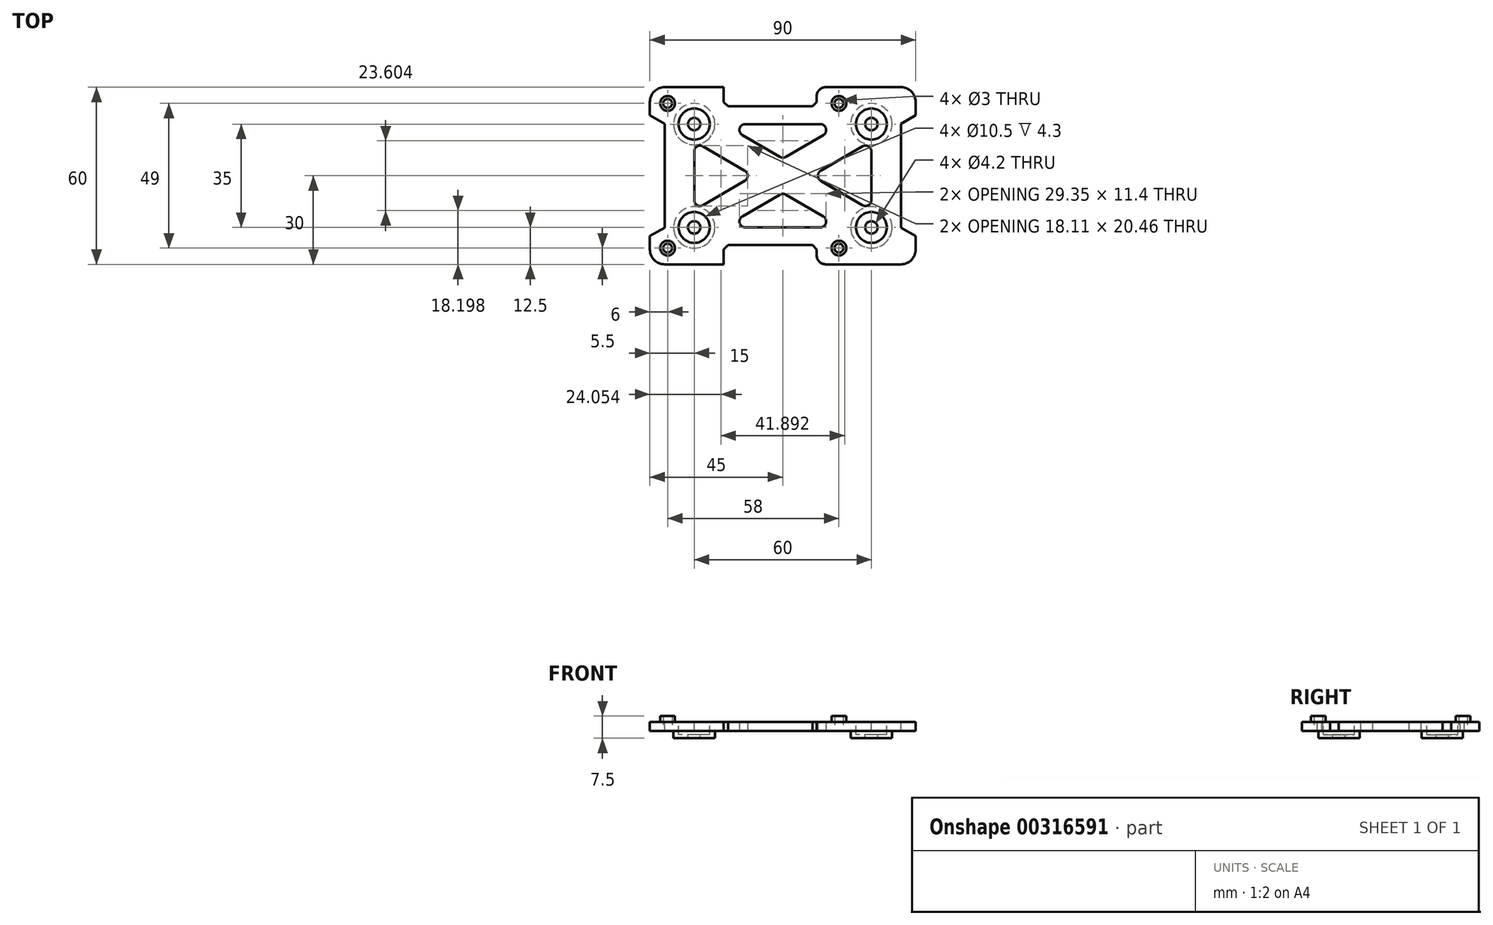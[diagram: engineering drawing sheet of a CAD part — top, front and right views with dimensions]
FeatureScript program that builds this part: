
annotation { "Feature Type Name" : "Feature", "Feature Type Description" : "" }
export const myFeature = defineFeature(function(context is Context, id is Id, definition is map)
    precondition{}
    {
        {
            var Q0;
            Q0=qCreatedBy(makeId("Top.planeOp"),FACE);
            var sketch = newSketch(context, id + "F0", { "sketchPlane" : qUnion([Q0])});
            skLineSegment(sketch, "E0.bottom", {"start": v(-45, 30) * mm, "end": v(45, 30) * mm});
            skLineSegment(sketch, "E0.top", {"start": v(-45, -30) * mm, "end": v(45, -30) * mm});
            skLineSegment(sketch, "E0.left", {"start": v(-45, 30) * mm, "end": v(-45, -30) * mm});
            skLineSegment(sketch, "E0.right", {"start": v(45, 30) * mm, "end": v(45, -30) * mm});
            skPoint(sketch, "E1", {"position": v(-45, 0) * mm});
            skPoint(sketch, "E2", {"position": v(0, 30) * mm});
            skSolve(sketch);
        }
        {
            var Q0;
            Q0=makeQuery(id+"F0.imprint","IMPRINT",FACE,{"disambiguationData":[TD([[makeQuery(id+"F0.imprint","IMPRINT",EDGE,{"derivedFrom":sQuery(id+"F0.wireOp",EDGE,"E0.bottom")}),-1.0]])]});
            extrude(context, id + "F1", {"entities" : qUnion([Q0]), "depth" : 3 * mm});
        }
        {
            var Q0;
            Q0=makeQuery(id+"F1.opExtrude","CAP_FACE",FACE,{"disambiguationData":[OSD([sQuery(id+"F0.wireOp",EDGE,"E0.bottom"),sQuery(id+"F0.wireOp",EDGE,"E0.top"),sQuery(id+"F0.wireOp",EDGE,"E0.left"),sQuery(id+"F0.wireOp",EDGE,"E0.right")])],"isStart":false});
            var sketch = newSketch(context, id + "F2", { "sketchPlane" : qUnion([Q0])});
            skLineSegment(sketch, "E3.bottom", {"start": v(-39, 24.5) * mm, "end": v(19, 24.5) * mm, "construction": true});
            skLineSegment(sketch, "E3.top", {"start": v(-39, -24.5) * mm, "end": v(19, -24.5) * mm, "construction": true});
            skLineSegment(sketch, "E3.left", {"start": v(-39, 24.5) * mm, "end": v(-39, -24.5) * mm, "construction": true});
            skLineSegment(sketch, "E3.right", {"start": v(19, 24.5) * mm, "end": v(19, -24.5) * mm, "construction": true});
            skLineSegment(sketch, "E4.bottom", {"start": v(-42.5, 28) * mm, "end": v(42.5, 28) * mm, "construction": true});
            skLineSegment(sketch, "E4.top", {"start": v(-42.5, -28) * mm, "end": v(42.5, -28) * mm, "construction": true});
            skLineSegment(sketch, "E4.left", {"start": v(-42.5, 28) * mm, "end": v(-42.5, -28) * mm, "construction": true});
            skLineSegment(sketch, "E4.right", {"start": v(42.5, 28) * mm, "end": v(42.5, -28) * mm, "construction": true});
            skPoint(sketch, "E5", {"position": v(-42.5, 0) * mm});
            skPoint(sketch, "E6", {"position": v(-39, 0) * mm});
            skPoint(sketch, "E7", {"position": v(0, 28) * mm});
            skCircle(sketch, "E8", {"center": v(-39, 24.5) * mm, "radius": 2.5 * mm});
            skCircle(sketch, "E9", {"center": v(19, 24.5) * mm, "radius": 2.5 * mm});
            skCircle(sketch, "E10", {"center": v(19, -24.5) * mm, "radius": 2.5 * mm});
            skCircle(sketch, "E11", {"center": v(-39, -24.5) * mm, "radius": 2.5 * mm});
            skSolve(sketch);
        }
        {
            var Q0;
            Q0=makeQuery(id+"F2.imprint","IMPRINT",FACE,{"disambiguationData":[TD([[makeQuery(id+"F2.imprint","IMPRINT",EDGE,{"derivedFrom":sQuery(id+"F2.wireOp",EDGE,"E8")}),1.0]])]});
            var Q1;
            Q1=makeQuery(id+"F2.imprint","IMPRINT",FACE,{"disambiguationData":[TD([[makeQuery(id+"F2.imprint","IMPRINT",EDGE,{"derivedFrom":sQuery(id+"F2.wireOp",EDGE,"E9")}),1.0]])]});
            var Q2;
            Q2=makeQuery(id+"F2.imprint","IMPRINT",FACE,{"disambiguationData":[TD([[makeQuery(id+"F2.imprint","IMPRINT",EDGE,{"derivedFrom":sQuery(id+"F2.wireOp",EDGE,"E10")}),1.0]])]});
            var Q3;
            Q3=makeQuery(id+"F2.imprint","IMPRINT",FACE,{"disambiguationData":[TD([[makeQuery(id+"F2.imprint","IMPRINT",EDGE,{"derivedFrom":sQuery(id+"F2.wireOp",EDGE,"E11")}),1.0]])]});
            extrude(context, id + "F3", {"entities" : qUnion([Q0, Q1, Q2, Q3]), "operationType" : NewBodyOperationType.ADD, "depth" : 2 * mm, "offsetDistance" : 25 * mm});
        }
        {
            var Q0;
            Q0=makeQuery(id+"F1.opExtrude","CAP_FACE",FACE,{"disambiguationData":[OSD([sQuery(id+"F0.wireOp",EDGE,"E0.bottom"),sQuery(id+"F0.wireOp",EDGE,"E0.top"),sQuery(id+"F0.wireOp",EDGE,"E0.left"),sQuery(id+"F0.wireOp",EDGE,"E0.right")])],"isStart":true});
            var sketch = newSketch(context, id + "F4", { "sketchPlane" : qUnion([Q0])});
            skCircle(sketch, "E12.0.0", {"center": v(-39, -24.5) * mm, "radius": 2.5 * mm, "construction": true});
            skCircle(sketch, "E13.0.0", {"center": v(-39, 24.5) * mm, "radius": 2.5 * mm, "construction": true});
            skCircle(sketch, "E14.0.0", {"center": v(19, 24.5) * mm, "radius": 2.5 * mm, "construction": true});
            skCircle(sketch, "E15.0", {"center": v(19, -24.5) * mm, "radius": 2.5 * mm, "construction": true});
            skCircle(sketch, "E16", {"center": v(-39, 24.5) * mm, "radius": 1.5 * mm});
            skCircle(sketch, "E17", {"center": v(19, 24.5) * mm, "radius": 1.5 * mm});
            skCircle(sketch, "E18", {"center": v(19, -24.5) * mm, "radius": 1.5 * mm});
            skCircle(sketch, "E19", {"center": v(-39, -24.5) * mm, "radius": 1.5 * mm});
            skSolve(sketch);
        }
        {
            var Q0;
            Q0=makeQuery(id+"F4.imprint","IMPRINT",FACE,{"disambiguationData":[TD([[makeQuery(id+"F4.imprint","IMPRINT",EDGE,{"derivedFrom":sQuery(id+"F4.wireOp",EDGE,"E16")}),1.0]])]});
            var Q1;
            Q1=makeQuery(id+"F4.imprint","IMPRINT",FACE,{"disambiguationData":[TD([[makeQuery(id+"F4.imprint","IMPRINT",EDGE,{"derivedFrom":sQuery(id+"F4.wireOp",EDGE,"E17")}),1.0]])]});
            var Q2;
            Q2=makeQuery(id+"F4.imprint","IMPRINT",FACE,{"disambiguationData":[TD([[makeQuery(id+"F4.imprint","IMPRINT",EDGE,{"derivedFrom":sQuery(id+"F4.wireOp",EDGE,"E18")}),1.0]])]});
            var Q3;
            Q3=makeQuery(id+"F4.imprint","IMPRINT",FACE,{"disambiguationData":[TD([[makeQuery(id+"F4.imprint","IMPRINT",EDGE,{"derivedFrom":sQuery(id+"F4.wireOp",EDGE,"E19")}),1.0]])]});
            var Q4;
            Q4=makeQuery(id+"F3.opExtrude","CAP_FACE",FACE,{"disambiguationData":[OSD([sQuery(id+"F2.wireOp",EDGE,"E11")])],"isStart":false});
            extrude(context, id + "F5", {"entities" : qUnion([Q0, Q1, Q2, Q3]), "operationType" : NewBodyOperationType.REMOVE, "endBound" : BoundingType.UP_TO_SURFACE, "oppositeDirection" : true, "endBoundEntityFace" : qUnion([Q4]), "depth" : 25 * mm});
        }
        {
            var Q0;
            Q0=makeQuery(id+"F1.opExtrude","CAP_FACE",FACE,{"disambiguationData":[OSD([sQuery(id+"F0.wireOp",EDGE,"E0.bottom"),sQuery(id+"F0.wireOp",EDGE,"E0.top"),sQuery(id+"F0.wireOp",EDGE,"E0.left"),sQuery(id+"F0.wireOp",EDGE,"E0.right")])],"isStart":true});
            var sketch = newSketch(context, id + "F6", { "sketchPlane" : qUnion([Q0])});
            skLineSegment(sketch, "E20.bottom", {"start": v(30, -17.5) * mm, "end": v(-30, -17.5) * mm, "construction": true});
            skLineSegment(sketch, "E20.top", {"start": v(30, 17.5) * mm, "end": v(-30, 17.5) * mm, "construction": true});
            skLineSegment(sketch, "E20.left", {"start": v(30, -17.5) * mm, "end": v(30, 17.5) * mm, "construction": true});
            skLineSegment(sketch, "E20.right", {"start": v(-30, -17.5) * mm, "end": v(-30, 17.5) * mm, "construction": true});
            skCircle(sketch, "E21", {"center": v(30, -17.5) * mm, "radius": 7 * mm});
            skCircle(sketch, "E22", {"center": v(-30, -17.5) * mm, "radius": 7 * mm});
            skCircle(sketch, "E23", {"center": v(-30, 17.5) * mm, "radius": 7 * mm});
            skCircle(sketch, "E24", {"center": v(30, 17.5) * mm, "radius": 7 * mm});
            skPoint(sketch, "E25", {"position": v(0, -17.5) * mm});
            skPoint(sketch, "E26", {"position": v(30, 0) * mm});
            skSolve(sketch);
        }
        {
            var Q0;
            Q0=makeQuery(id+"F6.imprint","IMPRINT",FACE,{"disambiguationData":[TD([[makeQuery(id+"F6.imprint","IMPRINT",EDGE,{"derivedFrom":sQuery(id+"F6.wireOp",EDGE,"E21")}),1.0]])]});
            var Q1;
            Q1=makeQuery(id+"F6.imprint","IMPRINT",FACE,{"disambiguationData":[TD([[makeQuery(id+"F6.imprint","IMPRINT",EDGE,{"derivedFrom":sQuery(id+"F6.wireOp",EDGE,"E24")}),1.0]])]});
            var Q2;
            Q2=makeQuery(id+"F6.imprint","IMPRINT",FACE,{"disambiguationData":[TD([[makeQuery(id+"F6.imprint","IMPRINT",EDGE,{"derivedFrom":sQuery(id+"F6.wireOp",EDGE,"E22")}),1.0]])]});
            var Q3;
            Q3=makeQuery(id+"F6.imprint","IMPRINT",FACE,{"disambiguationData":[TD([[makeQuery(id+"F6.imprint","IMPRINT",EDGE,{"derivedFrom":sQuery(id+"F6.wireOp",EDGE,"E23")}),1.0]])]});
            extrude(context, id + "F7", {"entities" : qUnion([Q0, Q1, Q2, Q3]), "operationType" : NewBodyOperationType.ADD, "depth" : 2.5 * mm});
        }
        {
            var Q0;
            Q0=makeQuery(id+"F1.opExtrude","CAP_FACE",FACE,{"disambiguationData":[OSD([sQuery(id+"F0.wireOp",EDGE,"E0.bottom"),sQuery(id+"F0.wireOp",EDGE,"E0.top"),sQuery(id+"F0.wireOp",EDGE,"E0.left"),sQuery(id+"F0.wireOp",EDGE,"E0.right")])],"isStart":false});
            var sketch = newSketch(context, id + "F8", { "sketchPlane" : qUnion([Q0])});
            skCircle(sketch, "E27.0.0", {"center": v(30, 17.5) * mm, "radius": 7 * mm, "construction": true});
            skCircle(sketch, "E28.0.0", {"center": v(30, -17.5) * mm, "radius": 7 * mm, "construction": true});
            skCircle(sketch, "E29.0.0", {"center": v(-30, -17.5) * mm, "radius": 7 * mm, "construction": true});
            skCircle(sketch, "E30.0.0", {"center": v(-30, 17.5) * mm, "radius": 7 * mm, "construction": true});
            skCircle(sketch, "E31", {"center": v(30, -17.5) * mm, "radius": 5.25 * mm});
            skCircle(sketch, "E32", {"center": v(-30, -17.5) * mm, "radius": 5.25 * mm});
            skCircle(sketch, "E33", {"center": v(-30, 17.5) * mm, "radius": 5.25 * mm});
            skCircle(sketch, "E34", {"center": v(30, 17.5) * mm, "radius": 5.25 * mm});
            skCircle(sketch, "E35", {"center": v(-30, -17.5) * mm, "radius": 2.1 * mm});
            skCircle(sketch, "E36", {"center": v(30, -17.5) * mm, "radius": 2.1 * mm});
            skCircle(sketch, "E37", {"center": v(30, 17.5) * mm, "radius": 2.1 * mm});
            skCircle(sketch, "E38", {"center": v(-30, 17.5) * mm, "radius": 2.1 * mm});
            skSolve(sketch);
        }
        {
            var Q0;
            Q0=makeQuery(id+"F8.imprint","IMPRINT",FACE,{"disambiguationData":[TD([[makeQuery(id+"F8.imprint","IMPRINT",EDGE,{"derivedFrom":sQuery(id+"F8.wireOp",EDGE,"E31")}),1.0]])]});
            var Q1;
            Q1=makeQuery(id+"F8.imprint","IMPRINT",FACE,{"disambiguationData":[TD([[makeQuery(id+"F8.imprint","IMPRINT",EDGE,{"derivedFrom":sQuery(id+"F8.wireOp",EDGE,"E32")}),1.0]])]});
            var Q2;
            Q2=makeQuery(id+"F8.imprint","IMPRINT",FACE,{"disambiguationData":[TD([[makeQuery(id+"F8.imprint","IMPRINT",EDGE,{"derivedFrom":sQuery(id+"F8.wireOp",EDGE,"E33")}),1.0]])]});
            var Q3;
            Q3=makeQuery(id+"F8.imprint","IMPRINT",FACE,{"disambiguationData":[TD([[makeQuery(id+"F8.imprint","IMPRINT",EDGE,{"derivedFrom":sQuery(id+"F8.wireOp",EDGE,"E34")}),1.0]])]});
            extrude(context, id + "F9", {"entities" : qUnion([Q0, Q1, Q2, Q3]), "operationType" : NewBodyOperationType.REMOVE, "oppositeDirection" : true, "depth" : 4.3 * mm});
        }
        {
            var Q0;
            Q0=makeQuery(id+"F8.imprint","IMPRINT",FACE,{"disambiguationData":[TD([[makeQuery(id+"F8.imprint","IMPRINT",EDGE,{"derivedFrom":sQuery(id+"F8.wireOp",EDGE,"E35")}),1.0]])]});
            var Q1;
            Q1=makeQuery(id+"F8.imprint","IMPRINT",FACE,{"disambiguationData":[TD([[makeQuery(id+"F8.imprint","IMPRINT",EDGE,{"derivedFrom":sQuery(id+"F8.wireOp",EDGE,"E38")}),1.0]])]});
            var Q2;
            Q2=makeQuery(id+"F8.imprint","IMPRINT",FACE,{"disambiguationData":[TD([[makeQuery(id+"F8.imprint","IMPRINT",EDGE,{"derivedFrom":sQuery(id+"F8.wireOp",EDGE,"E37")}),1.0]])]});
            var Q3;
            Q3=makeQuery(id+"F8.imprint","IMPRINT",FACE,{"disambiguationData":[TD([[makeQuery(id+"F8.imprint","IMPRINT",EDGE,{"derivedFrom":sQuery(id+"F8.wireOp",EDGE,"E36")}),1.0]])]});
            var Q4;
            Q4=makeQuery(id+"F7.opExtrude","CAP_FACE",FACE,{"disambiguationData":[OSD([sQuery(id+"F6.wireOp",EDGE,"E23")])],"isStart":false});
            extrude(context, id + "F10", {"entities" : qUnion([Q0, Q1, Q2, Q3]), "operationType" : NewBodyOperationType.REMOVE, "endBound" : BoundingType.UP_TO_SURFACE, "oppositeDirection" : true, "endBoundEntityFace" : qUnion([Q4]), "depth" : 25 * mm});
        }
        {
            var Q0;
            Q0=makeQuery(id+"F8.imprint","IMPRINT",FACE,{"disambiguationData":[TD([[makeQuery(id+"F8.imprint","IMPRINT",EDGE,{"derivedFrom":sQuery(id+"F8.wireOp",EDGE,"E31")}),-1.0]])]});
            var sketch = newSketch(context, id + "F11", { "sketchPlane" : qUnion([Q0])});
            skCircle(sketch, "E39.0.0", {"center": v(-30, 17.5) * mm, "radius": 5.25 * mm, "construction": true});
            skCircle(sketch, "E40.0.0", {"center": v(30, 17.5) * mm, "radius": 5.25 * mm, "construction": true});
            skCircle(sketch, "E41.0.0", {"center": v(30, -17.5) * mm, "radius": 5.25 * mm, "construction": true});
            skCircle(sketch, "E42.0", {"center": v(-30, -17.5) * mm, "radius": 5.25 * mm, "construction": true});
            skLineSegment(sketch, "E43.0.0", {"start": v(45, 30) * mm, "end": v(-45, 30) * mm, "construction": true});
            skLineSegment(sketch, "E43.0.1", {"start": v(-45, 30) * mm, "end": v(-45, -30) * mm, "construction": true});
            skLineSegment(sketch, "E43.0.2", {"start": v(-45, -30) * mm, "end": v(45, -30) * mm, "construction": true});
            skLineSegment(sketch, "E43.0.3", {"start": v(45, -30) * mm, "end": v(45, 30) * mm, "construction": true});
            skLineSegment(sketch, "E44", {"start": v(-30, 17.5) * mm, "end": v(30, -17.5) * mm, "construction": true});
            skLineSegment(sketch, "E45", {"start": v(30, 17.5) * mm, "end": v(-30, -17.5) * mm, "construction": true});
            skLineSegment(sketch, "E46", {"start": v(-30, 17.5) * mm, "end": v(-30, -17.5) * mm, "construction": true});
            skLineSegment(sketch, "E47", {"start": v(30, -17.5) * mm, "end": v(-30, -17.5) * mm, "construction": true});
            skLineSegment(sketch, "E48", {"start": v(30, -17.5) * mm, "end": v(30, 17.5) * mm, "construction": true});
            skLineSegment(sketch, "E49", {"start": v(30, 17.5) * mm, "end": v(-30, 17.5) * mm, "construction": true});
            skLineSegment(sketch, "E50", {"start": v(-30, 11.71) * mm, "end": v(-30, -11.71) * mm});
            skLineSegment(sketch, "E51", {"start": v(-30, -11.71) * mm, "end": v(-9.92, 0) * mm});
            skLineSegment(sketch, "E52", {"start": v(-9.92, 0) * mm, "end": v(-30, 11.71) * mm});
            skLineSegment(sketch, "E53", {"start": v(9.92, 0) * mm, "end": v(30, 11.71) * mm});
            skLineSegment(sketch, "E54", {"start": v(30, 11.71) * mm, "end": v(30, -11.71) * mm});
            skLineSegment(sketch, "E55", {"start": v(30, -11.71) * mm, "end": v(9.92, 0) * mm});
            skLineSegment(sketch, "E56", {"start": v(-20.08, 17.5) * mm, "end": v(0, 5.79) * mm});
            skLineSegment(sketch, "E57", {"start": v(0, 5.79) * mm, "end": v(20.08, 17.5) * mm});
            skLineSegment(sketch, "E58", {"start": v(20.08, 17.5) * mm, "end": v(-20.08, 17.5) * mm});
            skLineSegment(sketch, "E59", {"start": v(-20.08, -17.5) * mm, "end": v(0, -5.79) * mm});
            skLineSegment(sketch, "E60", {"start": v(0, -5.79) * mm, "end": v(20.08, -17.5) * mm});
            skLineSegment(sketch, "E61", {"start": v(20.08, -17.5) * mm, "end": v(-20.08, -17.5) * mm});
            skLineSegment(sketch, "E62", {"start": v(-45, 20.46) * mm, "end": v(-40, 17.54) * mm});
            skLineSegment(sketch, "E63", {"start": v(-40, 17.54) * mm, "end": v(-40, -17.54) * mm});
            skLineSegment(sketch, "E64", {"start": v(-40, -17.54) * mm, "end": v(-45, -20.46) * mm});
            skLineSegment(sketch, "E65", {"start": v(-45, -20.46) * mm, "end": v(-45, 20.46) * mm});
            skLineSegment(sketch, "E66", {"start": v(45, 20.46) * mm, "end": v(40, 17.54) * mm});
            skLineSegment(sketch, "E67", {"start": v(40, 17.54) * mm, "end": v(40, -17.54) * mm});
            skLineSegment(sketch, "E68", {"start": v(40, -17.54) * mm, "end": v(45, -20.46) * mm});
            skLineSegment(sketch, "E69", {"start": v(45, -20.46) * mm, "end": v(45, 20.46) * mm});
            skPoint(sketch, "E70", {"position": v(-45, 0) * mm});
            skPoint(sketch, "E71", {"position": v(45, 0) * mm});
            skLineSegment(sketch, "E72", {"start": v(-40, 17.54) * mm, "end": v(-30, 11.71) * mm, "construction": true});
            skLineSegment(sketch, "E73", {"start": v(30, 11.71) * mm, "end": v(40, 17.54) * mm, "construction": true});
            skLineSegment(sketch, "E74.bottom", {"start": v(-20.08, 30) * mm, "end": v(11.5, 30) * mm});
            skLineSegment(sketch, "E74.top", {"start": v(-20.08, 23.5) * mm, "end": v(11.5, 23.5) * mm});
            skLineSegment(sketch, "E74.left", {"start": v(-20.08, 30) * mm, "end": v(-20.08, 23.5) * mm});
            skLineSegment(sketch, "E74.right", {"start": v(11.5, 30) * mm, "end": v(11.5, 23.5) * mm});
            skLineSegment(sketch, "E75.bottom", {"start": v(-20.08, -30) * mm, "end": v(11.5, -30) * mm});
            skLineSegment(sketch, "E75.top", {"start": v(-20.08, -23.5) * mm, "end": v(11.5, -23.5) * mm});
            skLineSegment(sketch, "E75.left", {"start": v(-20.08, -30) * mm, "end": v(-20.08, -23.5) * mm});
            skLineSegment(sketch, "E75.right", {"start": v(11.5, -30) * mm, "end": v(11.5, -23.5) * mm});
            skSolve(sketch);
        }
        {
            var Q0;
            Q0=makeQuery(id+"F11.imprint","IMPRINT",FACE,{"disambiguationData":[TD([[makeQuery(id+"F11.imprint","IMPRINT",EDGE,{"derivedFrom":sQuery(id+"F11.wireOp",EDGE,"E62")}),-1.0]])]});
            var Q1;
            Q1=makeQuery(id+"F11.imprint","IMPRINT",FACE,{"disambiguationData":[TD([[makeQuery(id+"F11.imprint","IMPRINT",EDGE,{"derivedFrom":sQuery(id+"F11.wireOp",EDGE,"E50")}),1.0]])]});
            var Q2;
            Q2=makeQuery(id+"F11.imprint","IMPRINT",FACE,{"disambiguationData":[TD([[makeQuery(id+"F11.imprint","IMPRINT",EDGE,{"derivedFrom":sQuery(id+"F11.wireOp",EDGE,"E56")}),1.0]])]});
            var Q3;
            Q3=makeQuery(id+"F11.imprint","IMPRINT",FACE,{"disambiguationData":[TD([[makeQuery(id+"F11.imprint","IMPRINT",EDGE,{"derivedFrom":sQuery(id+"F11.wireOp",EDGE,"E59")}),-1.0]])]});
            var Q4;
            Q4=makeQuery(id+"F11.imprint","IMPRINT",FACE,{"disambiguationData":[TD([[makeQuery(id+"F11.imprint","IMPRINT",EDGE,{"derivedFrom":sQuery(id+"F11.wireOp",EDGE,"E53")}),-1.0]])]});
            var Q5;
            Q5=makeQuery(id+"F11.imprint","IMPRINT",FACE,{"disambiguationData":[TD([[makeQuery(id+"F11.imprint","IMPRINT",EDGE,{"derivedFrom":sQuery(id+"F11.wireOp",EDGE,"E66")}),1.0]])]});
            var Q6;
            Q6=makeQuery(id+"F11.imprint","IMPRINT",FACE,{"disambiguationData":[TD([[makeQuery(id+"F11.imprint","IMPRINT",EDGE,{"derivedFrom":sQuery(id+"F11.wireOp",EDGE,"E74.bottom")}),-1.0]])]});
            var Q7;
            Q7=makeQuery(id+"F11.imprint","IMPRINT",FACE,{"disambiguationData":[TD([[makeQuery(id+"F11.imprint","IMPRINT",EDGE,{"derivedFrom":sQuery(id+"F11.wireOp",EDGE,"E75.bottom")}),1.0]])]});
            var Q8;
            Q8=makeQuery(id+"F1.opExtrude","CAP_FACE",FACE,{"disambiguationData":[OSD([sQuery(id+"F0.wireOp",EDGE,"E0.bottom"),sQuery(id+"F0.wireOp",EDGE,"E0.top"),sQuery(id+"F0.wireOp",EDGE,"E0.left"),sQuery(id+"F0.wireOp",EDGE,"E0.right")])],"isStart":true});
            extrude(context, id + "F12", {"entities" : qUnion([Q0, Q1, Q2, Q3, Q4, Q5, Q6, Q7]), "operationType" : NewBodyOperationType.REMOVE, "endBound" : BoundingType.UP_TO_SURFACE, "oppositeDirection" : true, "endBoundEntityFace" : qUnion([Q8]), "depth" : 25 * mm});
        }
        {
            var Q0;
            Q0=makeQuery(id+"F12.boolean.opBoolean","COPY",EDGE,{"derivedFrom":makeQuery(id+"F12.opExtrude","SWEPT_EDGE",EDGE,{"disambiguationData":[OSD([sQuery(id+"F11.wireOp",EDGE,"E50"),sQuery(id+"F11.wireOp",EDGE,"E51")])]})});
            var Q1;
            Q1=makeQuery(id+"F12.boolean.opBoolean","COPY",EDGE,{"derivedFrom":makeQuery(id+"F12.opExtrude","SWEPT_EDGE",EDGE,{"disambiguationData":[OSD([sQuery(id+"F11.wireOp",EDGE,"E50"),sQuery(id+"F11.wireOp",EDGE,"E52")])]})});
            var Q2;
            Q2=makeQuery(id+"F12.boolean.opBoolean","COPY",EDGE,{"derivedFrom":makeQuery(id+"F12.opExtrude","SWEPT_EDGE",EDGE,{"disambiguationData":[OSD([sQuery(id+"F11.wireOp",EDGE,"E51"),sQuery(id+"F11.wireOp",EDGE,"E52")])]})});
            var Q3;
            Q3=makeQuery(id+"F12.boolean.opBoolean","COPY",EDGE,{"derivedFrom":makeQuery(id+"F12.opExtrude","SWEPT_EDGE",EDGE,{"disambiguationData":[OSD([sQuery(id+"F11.wireOp",EDGE,"E53"),sQuery(id+"F11.wireOp",EDGE,"E55")])]})});
            var Q4;
            Q4=makeQuery(id+"F12.boolean.opBoolean","COPY",EDGE,{"derivedFrom":makeQuery(id+"F12.opExtrude","SWEPT_EDGE",EDGE,{"disambiguationData":[OSD([sQuery(id+"F11.wireOp",EDGE,"E54"),sQuery(id+"F11.wireOp",EDGE,"E55")])]})});
            var Q5;
            Q5=makeQuery(id+"F12.boolean.opBoolean","COPY",EDGE,{"derivedFrom":makeQuery(id+"F12.opExtrude","SWEPT_EDGE",EDGE,{"disambiguationData":[OSD([sQuery(id+"F11.wireOp",EDGE,"E53"),sQuery(id+"F11.wireOp",EDGE,"E54")])]})});
            var Q6;
            Q6=makeQuery(id+"F12.boolean.opBoolean","COPY",EDGE,{"derivedFrom":makeQuery(id+"F12.opExtrude","SWEPT_EDGE",EDGE,{"disambiguationData":[OSD([sQuery(id+"F11.wireOp",EDGE,"E57"),sQuery(id+"F11.wireOp",EDGE,"E58")])]})});
            var Q7;
            Q7=makeQuery(id+"F12.boolean.opBoolean","COPY",EDGE,{"derivedFrom":makeQuery(id+"F12.opExtrude","SWEPT_EDGE",EDGE,{"disambiguationData":[OSD([sQuery(id+"F11.wireOp",EDGE,"E60"),sQuery(id+"F11.wireOp",EDGE,"E61")])]})});
            var Q8;
            Q8=makeQuery(id+"F12.boolean.opBoolean","COPY",EDGE,{"derivedFrom":makeQuery(id+"F12.opExtrude","SWEPT_EDGE",EDGE,{"disambiguationData":[OSD([sQuery(id+"F11.wireOp",EDGE,"E59"),sQuery(id+"F11.wireOp",EDGE,"E61")])]})});
            var Q9;
            Q9=makeQuery(id+"F12.boolean.opBoolean","COPY",EDGE,{"derivedFrom":makeQuery(id+"F12.opExtrude","SWEPT_EDGE",EDGE,{"disambiguationData":[OSD([sQuery(id+"F11.wireOp",EDGE,"E56"),sQuery(id+"F11.wireOp",EDGE,"E58")])]})});
            var Q10;
            Q10=makeQuery(id+"F12.boolean.opBoolean","COPY",EDGE,{"derivedFrom":makeQuery(id+"F12.opExtrude","SWEPT_EDGE",EDGE,{"disambiguationData":[OSD([sQuery(id+"F11.wireOp",EDGE,"E56"),sQuery(id+"F11.wireOp",EDGE,"E57")])]})});
            var Q11;
            Q11=makeQuery(id+"F12.boolean.opBoolean","COPY",EDGE,{"derivedFrom":makeQuery(id+"F12.opExtrude","SWEPT_EDGE",EDGE,{"disambiguationData":[OSD([sQuery(id+"F11.wireOp",EDGE,"E59"),sQuery(id+"F11.wireOp",EDGE,"E60")])]})});
            fillet(context, id + "F13", {"entities" : qUnion([Q0, Q1, Q2, Q3, Q4, Q5, Q6, Q7, Q8, Q9, Q10, Q11]), "radius" : 2 * mm, "tangentPropagation" : true, "allowEdgeOverflow" : false});
        }
        {
            var Q0;
            Q0=makeQuery(id+"F12.boolean.opBoolean","COPY",EDGE,{"derivedFrom":makeQuery(id+"F12.opExtrude","SWEPT_EDGE",EDGE,{"disambiguationData":[OSD([sQuery(id+"F11.wireOp",EDGE,"E75.top"),sQuery(id+"F11.wireOp",EDGE,"E75.right")])]})});
            var Q1;
            Q1=makeQuery(id+"F12.boolean.opBoolean","COPY",EDGE,{"derivedFrom":makeQuery(id+"F12.opExtrude","SWEPT_EDGE",EDGE,{"disambiguationData":[OSD([sQuery(id+"F11.wireOp",EDGE,"E75.top"),sQuery(id+"F11.wireOp",EDGE,"E75.left")])]})});
            var Q2;
            Q2=makeQuery(id+"F12.boolean.opBoolean","COPY",EDGE,{"derivedFrom":makeQuery(id+"F12.opExtrude","SWEPT_EDGE",EDGE,{"disambiguationData":[OSD([sQuery(id+"F11.wireOp",EDGE,"E74.top"),sQuery(id+"F11.wireOp",EDGE,"E74.right")])]})});
            var Q3;
            Q3=makeQuery(id+"F12.boolean.opBoolean","COPY",EDGE,{"derivedFrom":makeQuery(id+"F12.opExtrude","SWEPT_EDGE",EDGE,{"disambiguationData":[OSD([sQuery(id+"F11.wireOp",EDGE,"E74.top"),sQuery(id+"F11.wireOp",EDGE,"E74.left")])]})});
            chamfer(context, id + "F14", {"entities" : qUnion([Q0, Q1, Q2, Q3]), "width" : 1.5 * mm, "tangentPropagation" : true});
        }
        {
            var Q0;
            Q0=makeQuery(id+"F1.opExtrude","SWEPT_EDGE",EDGE,{"disambiguationData":[OSD([sQuery(id+"F0.wireOp",EDGE,"E0.top"),sQuery(id+"F0.wireOp",EDGE,"E0.right")])]});
            var Q1;
            Q1=makeQuery(id+"F1.opExtrude","SWEPT_EDGE",EDGE,{"disambiguationData":[OSD([sQuery(id+"F0.wireOp",EDGE,"E0.bottom"),sQuery(id+"F0.wireOp",EDGE,"E0.right")])]});
            var Q2;
            Q2=makeQuery(id+"F1.opExtrude","SWEPT_EDGE",EDGE,{"disambiguationData":[OSD([sQuery(id+"F0.wireOp",EDGE,"E0.bottom"),sQuery(id+"F0.wireOp",EDGE,"E0.left")])]});
            var Q3;
            Q3=makeQuery(id+"F1.opExtrude","SWEPT_EDGE",EDGE,{"disambiguationData":[OSD([sQuery(id+"F0.wireOp",EDGE,"E0.top"),sQuery(id+"F0.wireOp",EDGE,"E0.left")])]});
            fillet(context, id + "F15", {"entities" : qUnion([Q0, Q1, Q2, Q3]), "radius" : 5 * mm, "tangentPropagation" : true, "allowEdgeOverflow" : false});
        }
        {
            var Q0;
            Q0=makeQuery(id+"F12.boolean.opBoolean","COPY",EDGE,{"derivedFrom":makeQuery(id+"F12.opExtrude","SWEPT_EDGE",EDGE,{"disambiguationData":[OSD([sQuery(id+"F0.wireOp",EDGE,"E0.top"),sQuery(id+"F11.wireOp",EDGE,"E75.bottom"),sQuery(id+"F11.wireOp",EDGE,"E75.right")])]})});
            var Q1;
            Q1=makeQuery(id+"F12.boolean.opBoolean","COPY",EDGE,{"derivedFrom":makeQuery(id+"F12.opExtrude","SWEPT_EDGE",EDGE,{"disambiguationData":[OSD([sQuery(id+"F0.wireOp",EDGE,"E0.bottom"),sQuery(id+"F11.wireOp",EDGE,"E74.bottom"),sQuery(id+"F11.wireOp",EDGE,"E74.left")])]})});
            var Q2;
            Q2=makeQuery(id+"F12.boolean.opBoolean","COPY",EDGE,{"derivedFrom":makeQuery(id+"F12.opExtrude","SWEPT_EDGE",EDGE,{"disambiguationData":[OSD([sQuery(id+"F0.wireOp",EDGE,"E0.bottom"),sQuery(id+"F11.wireOp",EDGE,"E74.bottom"),sQuery(id+"F11.wireOp",EDGE,"E74.right")])]})});
            var Q3;
            Q3=makeQuery(id+"F12.boolean.opBoolean","COPY",EDGE,{"derivedFrom":makeQuery(id+"F12.opExtrude","SWEPT_EDGE",EDGE,{"disambiguationData":[OSD([sQuery(id+"F0.wireOp",EDGE,"E0.top"),sQuery(id+"F11.wireOp",EDGE,"E75.bottom"),sQuery(id+"F11.wireOp",EDGE,"E75.left")])]})});
            fillet(context, id + "F16", {"entities" : qUnion([Q0, Q1, Q2, Q3]), "radius" : 3 * mm, "tangentPropagation" : true, "allowEdgeOverflow" : false});
        }
    });
